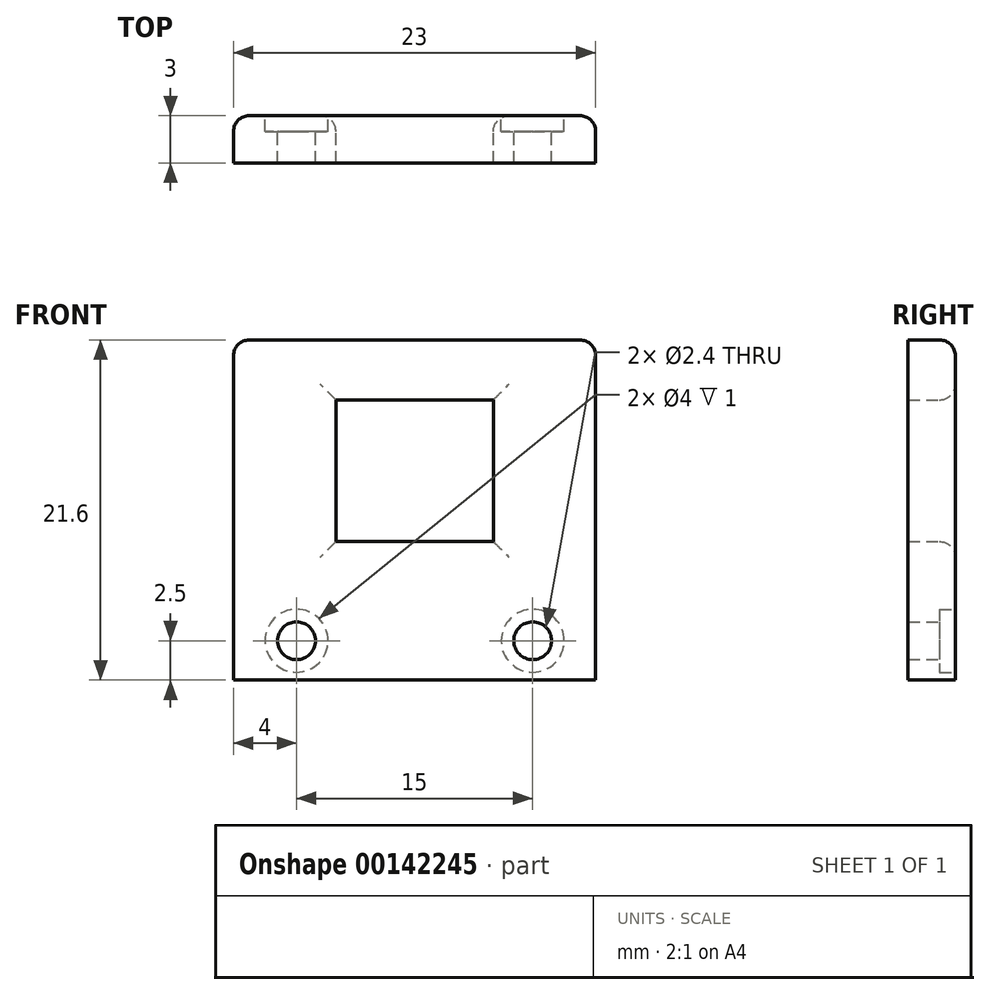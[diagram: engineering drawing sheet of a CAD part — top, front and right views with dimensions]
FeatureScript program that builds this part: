
annotation { "Feature Type Name" : "Feature", "Feature Type Description" : "" }
export const myFeature = defineFeature(function(context is Context, id is Id, definition is map)
    precondition{}
    {
        {
            var Q0;
            Q0=qCreatedBy(makeId("Front.planeOp"),FACE);
            var sketch = newSketch(context, id + "F0", { "sketchPlane" : qUnion([Q0])});
            skLineSegment(sketch, "E0.bottom", {"start": v(11.5, -10.8) * mm, "end": v(-11.5, -10.8) * mm});
            skLineSegment(sketch, "E0.top", {"start": v(11.5, 10.8) * mm, "end": v(-11.5, 10.8) * mm});
            skLineSegment(sketch, "E0.left", {"start": v(11.5, -10.8) * mm, "end": v(11.5, 10.8) * mm});
            skLineSegment(sketch, "E0.right", {"start": v(-11.5, -10.8) * mm, "end": v(-11.5, 10.8) * mm});
            skPoint(sketch, "E0.middle", {"position": v(0, 0) * mm});
            skLineSegment(sketch, "E1", {"start": v(11.5, -5.8) * mm, "end": v(-11.5, -5.8) * mm});
            skLineSegment(sketch, "E2.bottom", {"start": v(5, -2) * mm, "end": v(-5, -2) * mm});
            skLineSegment(sketch, "E2.top", {"start": v(5, 7) * mm, "end": v(-5, 7) * mm});
            skLineSegment(sketch, "E2.left", {"start": v(5, -2) * mm, "end": v(5, 7) * mm});
            skLineSegment(sketch, "E2.right", {"start": v(-5, -2) * mm, "end": v(-5, 7) * mm});
            skPoint(sketch, "E2.middle", {"position": v(0, 2.5) * mm});
            skLineSegment(sketch, "E3", {"start": v(-5, -5.8) * mm, "end": v(-5, -10.8) * mm});
            skLineSegment(sketch, "E4", {"start": v(5, -5.8) * mm, "end": v(5, -10.8) * mm});
            skPoint(sketch, "E5", {"position": v(-7.5, -8.3) * mm});
            skPoint(sketch, "E6", {"position": v(7.5, -8.3) * mm});
            skSolve(sketch);
        }
        {
            var Q0;
            Q0=makeQuery(id+"F0.imprint","IMPRINT",FACE,{"disambiguationData":[TD([[makeQuery(id+"F0.imprint","IMPRINT",EDGE,{"derivedFrom":sQuery(id+"F0.wireOp",EDGE,"E0.bottom")}),-1.0]])]});
            var Q1;
            {var subQ4=sQuery(id+"F0.wireOp",EDGE,"XXghgsD0-yHl0-RBd0-iBPM-BPhgWZTttXul");Q1=makeQuery(id+"F0.imprint","IMPRINT",FACE,{"disambiguationData":[TD([[makeQuery(id+"F0.imprint","IMPRINT",EDGE,{"derivedFrom":subQ4}),1.0]])]});}
            var Q2;
            {var subQ4=sQuery(id+"F0.wireOp",EDGE,"E0.left");var subQ5=sQuery(id+"F0.wireOp",EDGE,"E0.top");var subQ6=makeQuery(id+"F0.imprint","INTERSECT",VERTEX,{"derivedFrom":[subQ5,subQ4]});Q2=makeQuery(id+"F0.imprint","IMPRINT",FACE,{"disambiguationData":[TD([[makeQuery(id+"F0.imprint","IMPRINT",EDGE,{"disambiguationData":[TD([[subQ6,-1.0]])],"derivedFrom":subQ5}),1.0]])]});}
            var Q3;
            {var subQ7=sQuery(id+"F0.wireOp",EDGE,"rV4kGlWL-xtz4-GXx9-zthC-AsMHhICjl7HH");Q3=makeQuery(id+"F0.imprint","IMPRINT",FACE,{"disambiguationData":[TD([[makeQuery(id+"F0.imprint","IMPRINT",EDGE,{"derivedFrom":subQ7}),-1.0]])]});}
            var Q4;
            {var subQ3=sQuery(id+"F0.wireOp",EDGE,"XXghgsD0-yHl0-RBd0-iBPM-BPhgWZTttXul");Q4=makeQuery(id+"F0.imprint","IMPRINT",FACE,{"disambiguationData":[TD([[makeQuery(id+"F0.imprint","IMPRINT",EDGE,{"derivedFrom":subQ3}),-1.0]])]});}
            extrude(context, id + "F1", {"entities" : qUnion([Q0, Q1, Q2, Q3, Q4]), "depth" : 3 * mm});
        }
        {
            var Q0;
            Q0=sQuery(id+"F0.wireOp",VERTEX,"E6");
            var Q1;
            Q1=sQuery(id+"F0.wireOp",VERTEX,"E5");
            var Q2;
            Q2=makeQuery(id+"F1.opExtrude","SWEPT_BODY",BODY,{"disambiguationData":[OSD([sQuery(id+"F0.wireOp",EDGE,"E0.bottom"),sQuery(id+"F0.wireOp",EDGE,"E0.top"),sQuery(id+"F0.wireOp",EDGE,"E0.left"),sQuery(id+"F0.wireOp",EDGE,"E0.right"),sQuery(id+"F0.wireOp",EDGE,"E2.bottom"),sQuery(id+"F0.wireOp",EDGE,"E2.top"),sQuery(id+"F0.wireOp",EDGE,"E2.left"),sQuery(id+"F0.wireOp",EDGE,"E2.right")])]});
            hole(context, id + "F2", {"style" : HoleStyle.C_BORE, "endStyle" : HoleEndStyle.BLIND, "oppositeDirection" : true, "holeDiameter" : 2.4 * mm, "cBoreDiameter" : 4 * mm, "cBoreDepth" : 1 * mm, "holeDepth" : 3 * mm, "locations" : qUnion([Q0, Q1]), "scope" : qUnion([Q2])});
        }
        {
            var Q0;
            Q0=makeQuery(id+"F1.opExtrude","CAP_EDGE",EDGE,{"disambiguationData":[OSD([sQuery(id+"F0.wireOp",EDGE,"E0.right")])],"isStart":true});
            var Q1;
            Q1=makeQuery(id+"F1.opExtrude","CAP_EDGE",EDGE,{"disambiguationData":[OSD([sQuery(id+"F0.wireOp",EDGE,"E0.top")])],"isStart":true});
            var Q2;
            Q2=makeQuery(id+"F1.opExtrude","SWEPT_EDGE",EDGE,{"disambiguationData":[OSD([sQuery(id+"F0.wireOp",EDGE,"E0.top"),sQuery(id+"F0.wireOp",EDGE,"E0.left")])]});
            var Q3;
            Q3=makeQuery(id+"F1.opExtrude","SWEPT_EDGE",EDGE,{"disambiguationData":[OSD([sQuery(id+"F0.wireOp",EDGE,"E0.top"),sQuery(id+"F0.wireOp",EDGE,"E0.right")])]});
            var Q4;
            Q4=makeQuery(id+"F1.opExtrude","CAP_EDGE",EDGE,{"disambiguationData":[OSD([sQuery(id+"F0.wireOp",EDGE,"E0.left")])],"isStart":true});
            var Q5;
            Q5=makeQuery(id+"F1.opExtrude","CAP_EDGE",EDGE,{"disambiguationData":[OSD([sQuery(id+"F0.wireOp",EDGE,"E2.right")])],"isStart":true});
            var Q6;
            Q6=makeQuery(id+"F1.opExtrude","CAP_EDGE",EDGE,{"disambiguationData":[OSD([sQuery(id+"F0.wireOp",EDGE,"E2.top")])],"isStart":true});
            var Q7;
            Q7=makeQuery(id+"F1.opExtrude","CAP_EDGE",EDGE,{"disambiguationData":[OSD([sQuery(id+"F0.wireOp",EDGE,"E2.left")])],"isStart":true});
            var Q8;
            Q8=makeQuery(id+"F1.opExtrude","CAP_EDGE",EDGE,{"disambiguationData":[OSD([sQuery(id+"F0.wireOp",EDGE,"E2.bottom")])],"isStart":true});
            fillet(context, id + "F3", {"entities" : qUnion([Q0, Q1, Q2, Q3, Q4, Q5, Q6, Q7, Q8]), "radius" : 1 * mm, "tangentPropagation" : true, "allowEdgeOverflow" : false});
        }
    });
